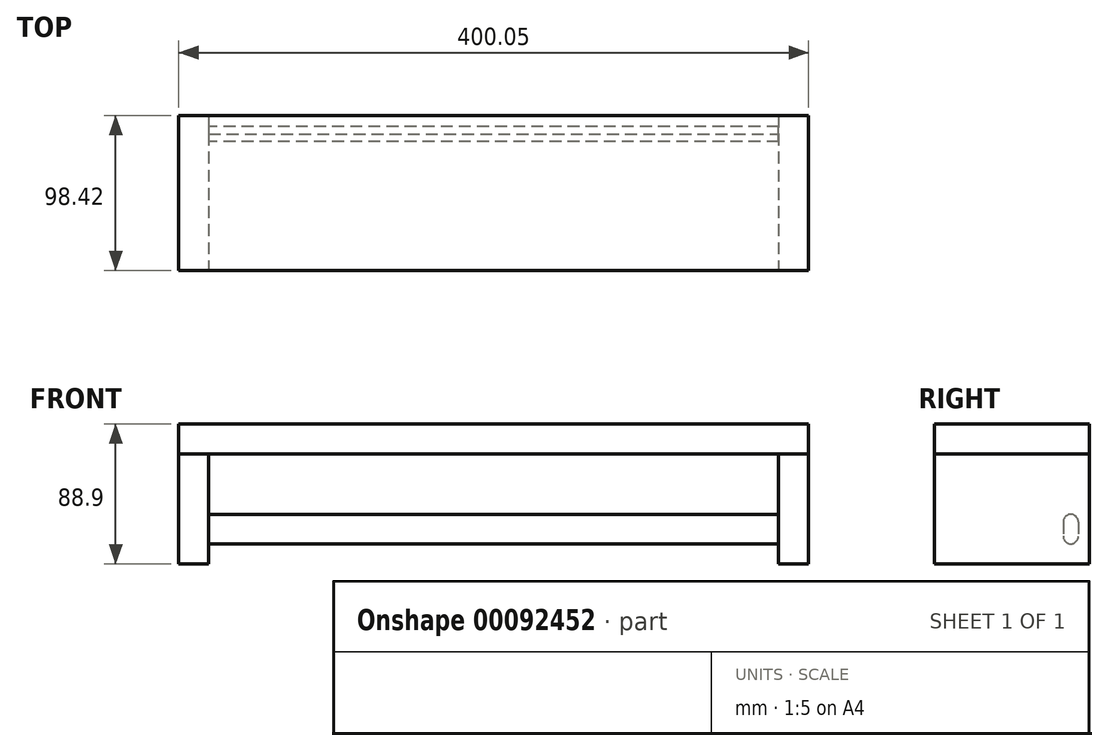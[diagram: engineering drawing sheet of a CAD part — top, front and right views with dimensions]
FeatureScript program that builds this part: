
annotation { "Feature Type Name" : "Feature", "Feature Type Description" : "" }
export const myFeature = defineFeature(function(context is Context, id is Id, definition is map)
    precondition{}
    {
        {
            var Q0;
            Q0=qCreatedBy(makeId("Top.planeOp"),FACE);
            var sketch = newSketch(context, id + "F0", { "sketchPlane" : qUnion([Q0])});
            skLineSegment(sketch, "E0.bottom", {"start": v(0, 0) * mm, "end": v(-400.05, 0) * mm});
            skLineSegment(sketch, "E0.top", {"start": v(0, -98.42) * mm, "end": v(-400.05, -98.42) * mm});
            skLineSegment(sketch, "E0.left", {"start": v(0, 0) * mm, "end": v(0, -98.42) * mm});
            skLineSegment(sketch, "E0.right", {"start": v(-400.05, 0) * mm, "end": v(-400.05, -98.42) * mm});
            skSolve(sketch);
        }
        {
            var Q0;
            Q0=makeQuery(id+"F0.imprint","IMPRINT",FACE,{"disambiguationData":[TD([[makeQuery(id+"F0.imprint","IMPRINT",EDGE,{"derivedFrom":sQuery(id+"F0.wireOp",EDGE,"E0.bottom")}),1.0]])]});
            extrude(context, id + "F1", {"entities" : qUnion([Q0]), "oppositeDirection" : true, "depth" : 19.05 * mm});
        }
        {
            var Q0;
            Q0=makeQuery(id+"F1.opExtrude","CAP_FACE",FACE,{"disambiguationData":[OSD([sQuery(id+"F0.wireOp",EDGE,"E0.bottom"),sQuery(id+"F0.wireOp",EDGE,"E0.top"),sQuery(id+"F0.wireOp",EDGE,"E0.left"),sQuery(id+"F0.wireOp",EDGE,"E0.right")])],"isStart":false});
            var sketch = newSketch(context, id + "F2", { "sketchPlane" : qUnion([Q0])});
            skLineSegment(sketch, "E1.bottom", {"start": v(0, 0) * mm, "end": v(-19.05, 0) * mm});
            skLineSegment(sketch, "E1.top", {"start": v(0, 98.42) * mm, "end": v(-19.05, 98.42) * mm});
            skLineSegment(sketch, "E1.left", {"start": v(0, 0) * mm, "end": v(0, 98.42) * mm});
            skLineSegment(sketch, "E1.right", {"start": v(-19.05, 0) * mm, "end": v(-19.05, 98.42) * mm});
            skLineSegment(sketch, "E2.bottom", {"start": v(-400.05, 0) * mm, "end": v(-381, 0) * mm});
            skLineSegment(sketch, "E2.top", {"start": v(-400.05, 98.42) * mm, "end": v(-381, 98.42) * mm});
            skLineSegment(sketch, "E2.left", {"start": v(-400.05, 0) * mm, "end": v(-400.05, 98.42) * mm});
            skLineSegment(sketch, "E2.right", {"start": v(-381, 0) * mm, "end": v(-381, 98.42) * mm});
            skSolve(sketch);
        }
        {
            var Q0;
            Q0=makeQuery(id+"F2.imprint","IMPRINT",FACE,{"disambiguationData":[TD([[makeQuery(id+"F2.imprint","IMPRINT",EDGE,{"derivedFrom":sQuery(id+"F2.wireOp",EDGE,"E1.bottom")}),-1.0]])]});
            var Q1;
            Q1=makeQuery(id+"F2.imprint","IMPRINT",FACE,{"disambiguationData":[TD([[makeQuery(id+"F2.imprint","IMPRINT",EDGE,{"derivedFrom":sQuery(id+"F2.wireOp",EDGE,"E2.bottom")}),-1.0]])]});
            extrude(context, id + "F3", {"entities" : qUnion([Q0, Q1]), "depth" : 69.85 * mm});
        }
        {
            var Q0;
            Q0=makeQuery(id+"F3.opExtrude","SWEPT_FACE",FACE,{"disambiguationData":[OSD([sQuery(id+"F2.wireOp",EDGE,"E2.right")])]});
            var sketch = newSketch(context, id + "F4", { "sketchPlane" : qUnion([Q0])});
            skLineSegment(sketch, "E3.bottom", {"start": v(-7.1, -76.33) * mm, "end": v(-16.62, -76.33) * mm});
            skLineSegment(sketch, "E3.top", {"start": v(-7.1, -57.28) * mm, "end": v(-16.62, -57.28) * mm});
            skLineSegment(sketch, "E3.left", {"start": v(-7.1, -76.33) * mm, "end": v(-7.1, -57.28) * mm});
            skLineSegment(sketch, "E3.right", {"start": v(-16.62, -76.33) * mm, "end": v(-16.62, -57.28) * mm});
            skSolve(sketch);
        }
        {
            var Q0;
            Q0=makeQuery(id+"F4.imprint","IMPRINT",FACE,{"disambiguationData":[TD([[makeQuery(id+"F4.imprint","IMPRINT",EDGE,{"derivedFrom":sQuery(id+"F4.wireOp",EDGE,"E3.bottom")}),-1.0]])]});
            extrude(context, id + "F5", {"entities" : qUnion([Q0]), "endBound" : BoundingType.UP_TO_NEXT, "depth" : 25.4 * mm});
        }
        {
            var Q0;
            Q0=makeQuery(id+"F5.opExtrude","SWEPT_EDGE",EDGE,{"disambiguationData":[OSD([sQuery(id+"F4.wireOp",EDGE,"E3.bottom"),sQuery(id+"F4.wireOp",EDGE,"E3.right")])]});
            var Q1;
            Q1=makeQuery(id+"F5.opExtrude","SWEPT_EDGE",EDGE,{"disambiguationData":[OSD([sQuery(id+"F4.wireOp",EDGE,"E3.bottom"),sQuery(id+"F4.wireOp",EDGE,"E3.left")])]});
            var Q2;
            Q2=makeQuery(id+"F5.opExtrude","SWEPT_EDGE",EDGE,{"disambiguationData":[OSD([sQuery(id+"F4.wireOp",EDGE,"E3.top"),sQuery(id+"F4.wireOp",EDGE,"E3.right")])]});
            var Q3;
            Q3=makeQuery(id+"F5.opExtrude","SWEPT_EDGE",EDGE,{"disambiguationData":[OSD([sQuery(id+"F4.wireOp",EDGE,"E3.top"),sQuery(id+"F4.wireOp",EDGE,"E3.left")])]});
            fillet(context, id + "F6", {"entities" : qUnion([Q0, Q1, Q2, Q3]), "radius" : 5.08 * mm, "tangentPropagation" : true, "allowEdgeOverflow" : false});
        }
    });
